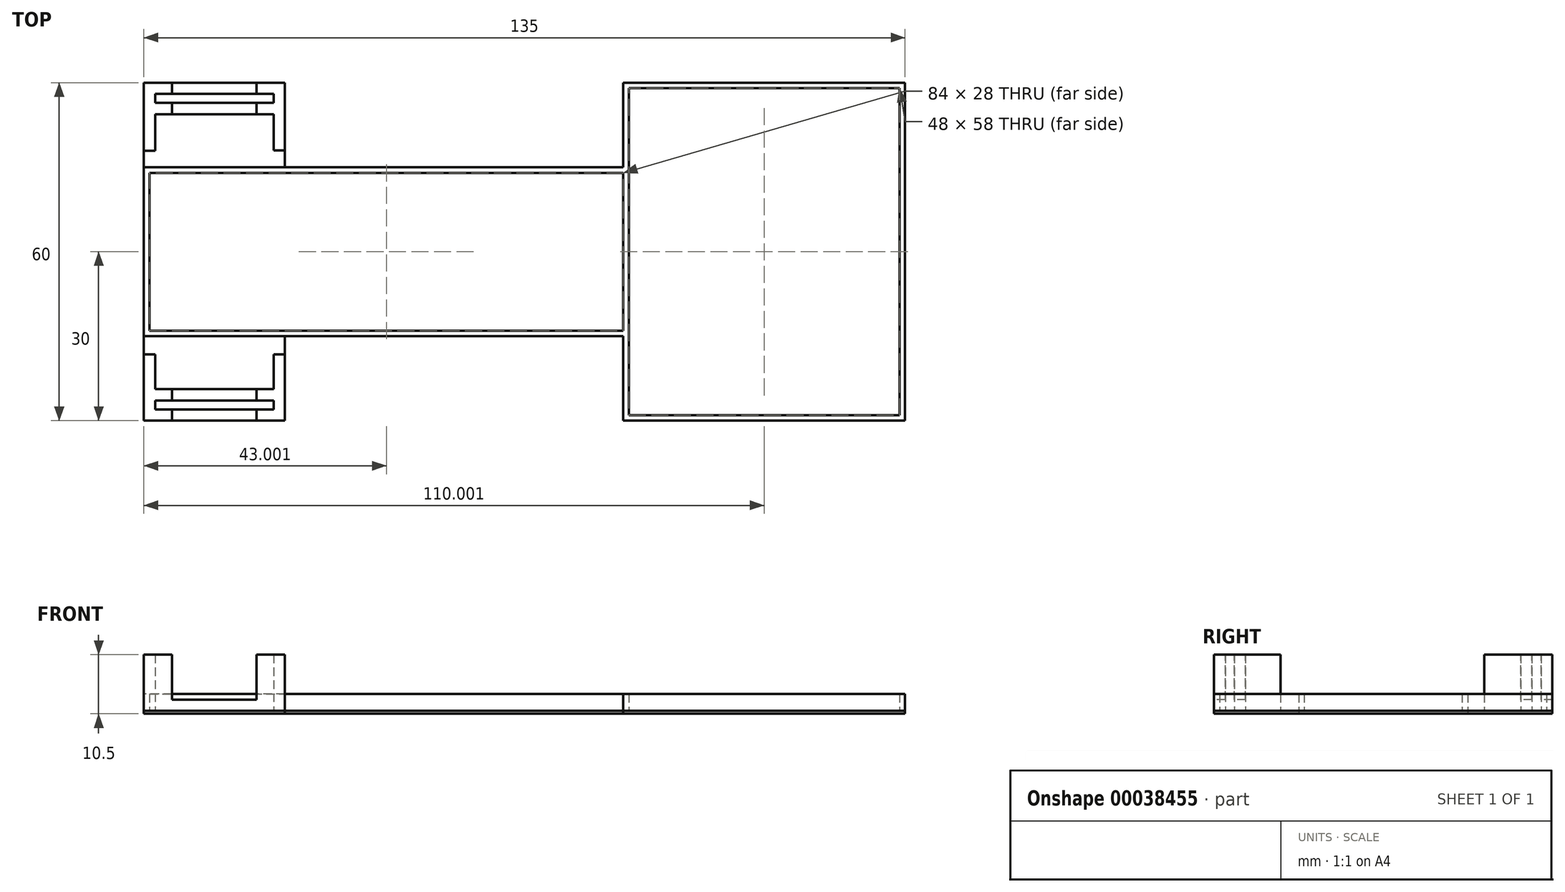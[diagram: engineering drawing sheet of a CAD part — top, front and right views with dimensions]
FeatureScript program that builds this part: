
annotation { "Feature Type Name" : "Feature", "Feature Type Description" : "" }
export const myFeature = defineFeature(function(context is Context, id is Id, definition is map)
    precondition{}
    {
        {
            var Q0;
            Q0=qCreatedBy(makeId("Top.planeOp"),FACE);
            var sketch = newSketch(context, id + "F0", { "sketchPlane" : qUnion([Q0])});
            skLineSegment(sketch, "E0.bottom", {"start": v(-50.48, 15) * mm, "end": v(9.52, 15) * mm});
            skLineSegment(sketch, "E0.top", {"start": v(-50.48, -15) * mm, "end": v(9.52, -15) * mm});
            skLineSegment(sketch, "E0.left", {"start": v(-50.48, 15) * mm, "end": v(-50.48, -15) * mm});
            skLineSegment(sketch, "E0.right", {"start": v(9.52, 15) * mm, "end": v(9.52, -15) * mm});
            skLineSegment(sketch, "E1.bottom", {"start": v(-75.48, 30) * mm, "end": v(-50.48, 30) * mm});
            skLineSegment(sketch, "E1.top", {"start": v(-75.48, -30) * mm, "end": v(-50.48, -30) * mm});
            skLineSegment(sketch, "E1.left", {"start": v(-75.48, 30) * mm, "end": v(-75.48, -30) * mm});
            skLineSegment(sketch, "E1.right", {"start": v(-50.48, 30) * mm, "end": v(-50.48, -30) * mm});
            skLineSegment(sketch, "E2.bottom", {"start": v(9.52, 30) * mm, "end": v(59.52, 30) * mm});
            skLineSegment(sketch, "E2.top", {"start": v(9.52, -30) * mm, "end": v(59.52, -30) * mm});
            skLineSegment(sketch, "E2.left", {"start": v(9.52, 30) * mm, "end": v(9.52, -30) * mm});
            skLineSegment(sketch, "E2.right", {"start": v(59.52, 30) * mm, "end": v(59.52, -30) * mm});
            skLineSegment(sketch, "E3.bottom", {"start": v(-59.52, 30) * mm, "end": v(59.52, 30) * mm, "construction": true});
            skLineSegment(sketch, "E3.top", {"start": v(-59.52, -30) * mm, "end": v(59.52, -30) * mm, "construction": true});
            skLineSegment(sketch, "E3.left", {"start": v(-59.52, 30) * mm, "end": v(-59.52, -30) * mm, "construction": true});
            skLineSegment(sketch, "E3.right", {"start": v(59.52, 30) * mm, "end": v(59.52, -30) * mm, "construction": true});
            skLineSegment(sketch, "E4", {"start": v(-59.52, 0) * mm, "end": v(59.52, 0) * mm, "construction": true});
            skLineSegment(sketch, "E5", {"start": v(0, 30) * mm, "end": v(0, -30) * mm, "construction": true});
            skLineSegment(sketch, "E6", {"start": v(-9.1, 15) * mm, "end": v(-9.1, -15) * mm, "construction": true});
            skLineSegment(sketch, "E7", {"start": v(-75.48, 0) * mm, "end": v(-9.1, 0) * mm, "construction": true});
            skSolve(sketch);
        }
        {
            var Q0;
            Q0 = qSketchRegion(id + "F0", true);
            extrude(context, id + "F1", {"entities" : qUnion([Q0]), "depth" : 0.5 * mm});
        }
        {
            var Q0;
            Q0=makeQuery(id+"F1.opExtrude","CAP_FACE",FACE,{"disambiguationData":[OSD([sQuery(id+"F0.wireOp",EDGE,"E0.bottom"),sQuery(id+"F0.wireOp",EDGE,"E0.top"),sQuery(id+"F0.wireOp",EDGE,"E1.bottom"),sQuery(id+"F0.wireOp",EDGE,"E1.top"),sQuery(id+"F0.wireOp",EDGE,"E1.left"),sQuery(id+"F0.wireOp",EDGE,"E1.right"),sQuery(id+"F0.wireOp",EDGE,"E2.bottom"),sQuery(id+"F0.wireOp",EDGE,"E2.top"),sQuery(id+"F0.wireOp",EDGE,"E2.left"),sQuery(id+"F0.wireOp",EDGE,"E2.right")])],"isStart":false});
            var sketch = newSketch(context, id + "F2", { "sketchPlane" : qUnion([Q0])});
            skLineSegment(sketch, "E8", {"start": v(59.52, 14) * mm, "end": v(-75.48, 14) * mm, "construction": true});
            skLineSegment(sketch, "E9", {"start": v(59.52, -14) * mm, "end": v(-75.48, -14) * mm, "construction": true});
            skLineSegment(sketch, "E10", {"start": v(10.52, 30) * mm, "end": v(10.52, -30) * mm, "construction": true});
            skLineSegment(sketch, "E11", {"start": v(9.52, 30) * mm, "end": v(9.52, -30) * mm, "construction": true});
            skLineSegment(sketch, "E12", {"start": v(-50.48, 15) * mm, "end": v(-75.48, 15) * mm, "construction": true});
            skLineSegment(sketch, "E13", {"start": v(-50.48, -15) * mm, "end": v(-75.48, -15) * mm, "construction": true});
            skLineSegment(sketch, "E14", {"start": v(-75.48, 15) * mm, "end": v(9.52, 15) * mm});
            skLineSegment(sketch, "E15", {"start": v(9.52, 15) * mm, "end": v(9.52, 30) * mm});
            skLineSegment(sketch, "E16", {"start": v(59.52, 30) * mm, "end": v(9.52, 30) * mm});
            skLineSegment(sketch, "E17", {"start": v(59.52, 30) * mm, "end": v(59.52, -30) * mm});
            skLineSegment(sketch, "E18", {"start": v(59.52, -30) * mm, "end": v(9.52, -30) * mm});
            skLineSegment(sketch, "E19", {"start": v(9.52, -30) * mm, "end": v(9.52, -15) * mm});
            skLineSegment(sketch, "E20", {"start": v(9.52, -15) * mm, "end": v(-75.48, -15) * mm});
            skLineSegment(sketch, "E21", {"start": v(-75.48, -15) * mm, "end": v(-75.48, 15) * mm});
            skLineSegment(sketch, "E22.bottom", {"start": v(-74.48, 14) * mm, "end": v(9.52, 14) * mm});
            skLineSegment(sketch, "E22.top", {"start": v(-74.48, -14) * mm, "end": v(9.52, -14) * mm});
            skLineSegment(sketch, "E22.left", {"start": v(-74.48, 14) * mm, "end": v(-74.48, -14) * mm});
            skLineSegment(sketch, "E22.right", {"start": v(9.52, 14) * mm, "end": v(9.52, -14) * mm});
            skLineSegment(sketch, "E23.bottom", {"start": v(10.52, 29) * mm, "end": v(58.52, 29) * mm});
            skLineSegment(sketch, "E23.top", {"start": v(10.52, -29) * mm, "end": v(58.52, -29) * mm});
            skLineSegment(sketch, "E23.left", {"start": v(10.52, 29) * mm, "end": v(10.52, -29) * mm});
            skLineSegment(sketch, "E23.right", {"start": v(58.52, 29) * mm, "end": v(58.52, -29) * mm});
            skSolve(sketch);
        }
        {
            var Q0;
            Q0 = qSketchRegion(id + "F2", true);
            extrude(context, id + "F3", {"entities" : qUnion([Q0]), "depth" : 3 * mm});
        }
        {
            var Q0;
            Q0=makeQuery(id+"F1.opExtrude","CAP_FACE",FACE,{"disambiguationData":[OSD([sQuery(id+"F0.wireOp",EDGE,"E0.bottom"),sQuery(id+"F0.wireOp",EDGE,"E0.top"),sQuery(id+"F0.wireOp",EDGE,"E1.bottom"),sQuery(id+"F0.wireOp",EDGE,"E1.top"),sQuery(id+"F0.wireOp",EDGE,"E1.left"),sQuery(id+"F0.wireOp",EDGE,"E1.right"),sQuery(id+"F0.wireOp",EDGE,"E2.bottom"),sQuery(id+"F0.wireOp",EDGE,"E2.top"),sQuery(id+"F0.wireOp",EDGE,"E2.left"),sQuery(id+"F0.wireOp",EDGE,"E2.right")])],"isStart":false});
            var sketch = newSketch(context, id + "F4", { "sketchPlane" : qUnion([Q0])});
            skLineSegment(sketch, "E24", {"start": v(-75.48, 24.4) * mm, "end": v(-50.48, 24.4) * mm, "construction": true});
            skLineSegment(sketch, "E25", {"start": v(-73.48, 30) * mm, "end": v(-73.48, -30) * mm, "construction": true});
            skLineSegment(sketch, "E26", {"start": v(-52.48, 30) * mm, "end": v(-52.48, -30) * mm, "construction": true});
            skLineSegment(sketch, "E27", {"start": v(-75.48, -24.4) * mm, "end": v(-50.48, -24.4) * mm, "construction": true});
            skLineSegment(sketch, "E28", {"start": v(-75.48, -30) * mm, "end": v(-50.48, -30) * mm});
            skLineSegment(sketch, "E29", {"start": v(-50.48, -30) * mm, "end": v(-50.48, -18.2) * mm});
            skLineSegment(sketch, "E30", {"start": v(-50.48, -18.2) * mm, "end": v(-52.48, -18.2) * mm});
            skLineSegment(sketch, "E31", {"start": v(-52.48, -18.2) * mm, "end": v(-52.48, -24.4) * mm});
            skLineSegment(sketch, "E32", {"start": v(-52.48, -24.4) * mm, "end": v(-73.48, -24.4) * mm});
            skLineSegment(sketch, "E33", {"start": v(-73.48, -24.4) * mm, "end": v(-73.48, -18.2) * mm});
            skLineSegment(sketch, "E34", {"start": v(-73.48, -18.2) * mm, "end": v(-75.48, -18.2) * mm});
            skLineSegment(sketch, "E35", {"start": v(-75.48, -18.2) * mm, "end": v(-75.48, -30) * mm});
            skLineSegment(sketch, "E36", {"start": v(-75.48, 30) * mm, "end": v(-50.48, 30) * mm});
            skLineSegment(sketch, "E37", {"start": v(-50.48, 30) * mm, "end": v(-50.48, 17.94) * mm});
            skLineSegment(sketch, "E38", {"start": v(-50.48, 17.94) * mm, "end": v(-52.48, 17.94) * mm});
            skLineSegment(sketch, "E39", {"start": v(-52.48, 17.94) * mm, "end": v(-52.48, 24.4) * mm});
            skLineSegment(sketch, "E40", {"start": v(-52.48, 24.4) * mm, "end": v(-73.48, 24.4) * mm});
            skLineSegment(sketch, "E41", {"start": v(-73.48, 24.4) * mm, "end": v(-73.48, 17.93) * mm});
            skLineSegment(sketch, "E42", {"start": v(-73.48, 17.93) * mm, "end": v(-75.48, 17.93) * mm});
            skLineSegment(sketch, "E43", {"start": v(-75.48, 17.93) * mm, "end": v(-75.48, 30) * mm});
            skLineSegment(sketch, "E44", {"start": v(-75.48, 28) * mm, "end": v(-50.48, 28) * mm, "construction": true});
            skLineSegment(sketch, "E45", {"start": v(-75.48, 26.4) * mm, "end": v(-50.48, 26.4) * mm, "construction": true});
            skLineSegment(sketch, "E46.bottom", {"start": v(-73.48, 28) * mm, "end": v(-52.48, 28) * mm});
            skLineSegment(sketch, "E46.top", {"start": v(-73.48, 26.4) * mm, "end": v(-52.48, 26.4) * mm});
            skLineSegment(sketch, "E46.left", {"start": v(-73.48, 28) * mm, "end": v(-73.48, 26.4) * mm});
            skLineSegment(sketch, "E46.right", {"start": v(-52.48, 28) * mm, "end": v(-52.48, 26.4) * mm});
            skLineSegment(sketch, "E47", {"start": v(-75.48, -26.4) * mm, "end": v(-50.48, -26.4) * mm, "construction": true});
            skLineSegment(sketch, "E48", {"start": v(-75.48, -28) * mm, "end": v(-50.48, -28) * mm, "construction": true});
            skLineSegment(sketch, "E49.bottom", {"start": v(-73.48, -26.4) * mm, "end": v(-52.48, -26.4) * mm});
            skLineSegment(sketch, "E49.top", {"start": v(-73.48, -28) * mm, "end": v(-52.48, -28) * mm});
            skLineSegment(sketch, "E49.left", {"start": v(-73.48, -26.4) * mm, "end": v(-73.48, -28) * mm});
            skLineSegment(sketch, "E49.right", {"start": v(-52.48, -26.4) * mm, "end": v(-52.48, -28) * mm});
            skSolve(sketch);
        }
        {
            var Q0;
            Q0 = qSketchRegion(id + "F4", true);
            extrude(context, id + "F5", {"entities" : qUnion([Q0]), "depth" : 10 * mm});
        }
        {
            var Q0;
            Q0=makeQuery(id+"F5.opExtrude","CAP_FACE",FACE,{"disambiguationData":[OSD([sQuery(id+"F4.wireOp",EDGE,"E36"),sQuery(id+"F4.wireOp",EDGE,"E37"),sQuery(id+"F4.wireOp",EDGE,"E38"),sQuery(id+"F4.wireOp",EDGE,"E39"),sQuery(id+"F4.wireOp",EDGE,"E40"),sQuery(id+"F4.wireOp",EDGE,"E41"),sQuery(id+"F4.wireOp",EDGE,"E42"),sQuery(id+"F4.wireOp",EDGE,"E43"),sQuery(id+"F4.wireOp",EDGE,"E46.bottom"),sQuery(id+"F4.wireOp",EDGE,"E46.top"),sQuery(id+"F4.wireOp",EDGE,"E46.left"),sQuery(id+"F4.wireOp",EDGE,"E46.right")])],"isStart":false});
            var sketch = newSketch(context, id + "F6", { "sketchPlane" : qUnion([Q0])});
            skLineSegment(sketch, "E50", {"start": v(-70.48, 30) * mm, "end": v(-70.48, 24.4) * mm, "construction": true});
            skLineSegment(sketch, "E51", {"start": v(-55.48, 30) * mm, "end": v(-55.48, 24.4) * mm, "construction": true});
            skLineSegment(sketch, "E52.bottom", {"start": v(-70.48, 30) * mm, "end": v(-55.48, 30) * mm});
            skLineSegment(sketch, "E52.top", {"start": v(-70.48, 24.4) * mm, "end": v(-55.48, 24.4) * mm});
            skLineSegment(sketch, "E52.left", {"start": v(-70.48, 30) * mm, "end": v(-70.48, 24.4) * mm});
            skLineSegment(sketch, "E52.right", {"start": v(-55.48, 30) * mm, "end": v(-55.48, 24.4) * mm});
            skSolve(sketch);
        }
        {
            var Q0;
            Q0 = qSketchRegion(id + "F6", true);
            extrude(context, id + "F7", {"entities" : qUnion([Q0]), "operationType" : NewBodyOperationType.REMOVE, "oppositeDirection" : true, "depth" : 8 * mm});
        }
        {
            var Q0;
            Q0=makeQuery(id+"F5.opExtrude","CAP_FACE",FACE,{"disambiguationData":[OSD([sQuery(id+"F4.wireOp",EDGE,"E28"),sQuery(id+"F4.wireOp",EDGE,"E29"),sQuery(id+"F4.wireOp",EDGE,"E30"),sQuery(id+"F4.wireOp",EDGE,"E31"),sQuery(id+"F4.wireOp",EDGE,"E32"),sQuery(id+"F4.wireOp",EDGE,"E33"),sQuery(id+"F4.wireOp",EDGE,"E34"),sQuery(id+"F4.wireOp",EDGE,"E35"),sQuery(id+"F4.wireOp",EDGE,"E49.bottom"),sQuery(id+"F4.wireOp",EDGE,"E49.top"),sQuery(id+"F4.wireOp",EDGE,"E49.left"),sQuery(id+"F4.wireOp",EDGE,"E49.right")])],"isStart":false});
            var sketch = newSketch(context, id + "F8", { "sketchPlane" : qUnion([Q0])});
            skLineSegment(sketch, "E53", {"start": v(-70.48, -24.4) * mm, "end": v(-70.48, -30) * mm, "construction": true});
            skLineSegment(sketch, "E54", {"start": v(-55.48, -24.4) * mm, "end": v(-55.48, -30) * mm, "construction": true});
            skLineSegment(sketch, "E55.bottom", {"start": v(-70.48, -24.4) * mm, "end": v(-55.48, -24.4) * mm});
            skLineSegment(sketch, "E55.top", {"start": v(-70.48, -30) * mm, "end": v(-55.48, -30) * mm});
            skLineSegment(sketch, "E55.left", {"start": v(-70.48, -24.4) * mm, "end": v(-70.48, -30) * mm});
            skLineSegment(sketch, "E55.right", {"start": v(-55.48, -24.4) * mm, "end": v(-55.48, -30) * mm});
            skSolve(sketch);
        }
        {
            var Q0;
            Q0 = qSketchRegion(id + "F8", true);
            extrude(context, id + "F9", {"entities" : qUnion([Q0]), "operationType" : NewBodyOperationType.REMOVE, "oppositeDirection" : true, "depth" : 8 * mm});
        }
    });
